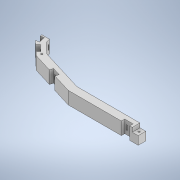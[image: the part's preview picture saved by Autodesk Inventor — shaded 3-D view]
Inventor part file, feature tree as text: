
AUTODESK INVENTOR PART (.ipt)
format: ipt  version: 2020 (Build 240168000, 168)  size: 330,752 bytes
history: native  units: mm
features: sketch x12, extrude x10, projected_geometry x8, hole x2, other x1
ambient origin geometry x8: Origin, YZ Plane, XZ Plane, XY Plane, X Axis, Y Axis, Z Axis, Center Point
bodies: Body1 (feature_tree)
feature tree (33):
  other  "솔리드1"
  extrude  "돌출1"  Depth=657.5mm
  extrude  "돌출2"  Depth=667.5mm
  extrude  "돌출3"  Depth=585.0mm
  extrude  "돌출4"  Depth=0.872665mm
  extrude  "돌출5"  Depth=1299.898854mm
  extrude  "돌출6"  Depth=2.356194mm
  extrude  "돌출7"  Depth=2.356194mm
  extrude  "돌출8"  Depth=999.812583mm
  extrude  "돌출9"  Depth=2.356194mm
  extrude  "돌출10"  Depth=2.356194mm
  hole  "구멍1"  [1 undecoded]
  hole  "구멍2"  [1 undecoded]
  sketch  "스케치1"
  sketch  "스케치2"
  sketch  "스케치3"
  projected_geometry  "투영된 루프1"
  sketch  "스케치5"
  projected_geometry  "투영된 루프3"
  sketch  "스케치6"
  projected_geometry  "투영된 루프4"
  sketch  "스케치7"
  projected_geometry  "투영된 루프5"
  sketch  "스케치8"
  projected_geometry  "투영된 루프6"
  sketch  "스케치9"
  projected_geometry  "투영된 루프7"
  sketch  "스케치10"
  projected_geometry  "투영된 루프8"
  sketch  "스케치11"
  projected_geometry  "투영된 루프9"
  sketch  "스케치12"
  sketch  "스케치13"
note: 2 required parameter values undecoded (feature->parameter linkage not recoverable at this tier; creation-order binding heuristic only, values carry confidence <= 0.55)
